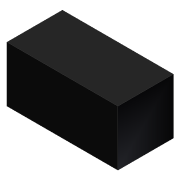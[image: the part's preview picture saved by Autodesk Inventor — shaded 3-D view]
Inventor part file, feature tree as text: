
AUTODESK INVENTOR PART (.ipt)
format: ipt  version: unknown  size: 166,400 bytes
history: native  units: mm
features: extrude x1, sketch x1
ambient origin geometry x8: Origin, YZ Plane, XZ Plane, XY Plane, X Axis, Y Axis, Z Axis, Center Point
feature tree (2):
  extrude  "Выдавливание2"  Depth=3.0mm
  sketch  "Эскиз2"
